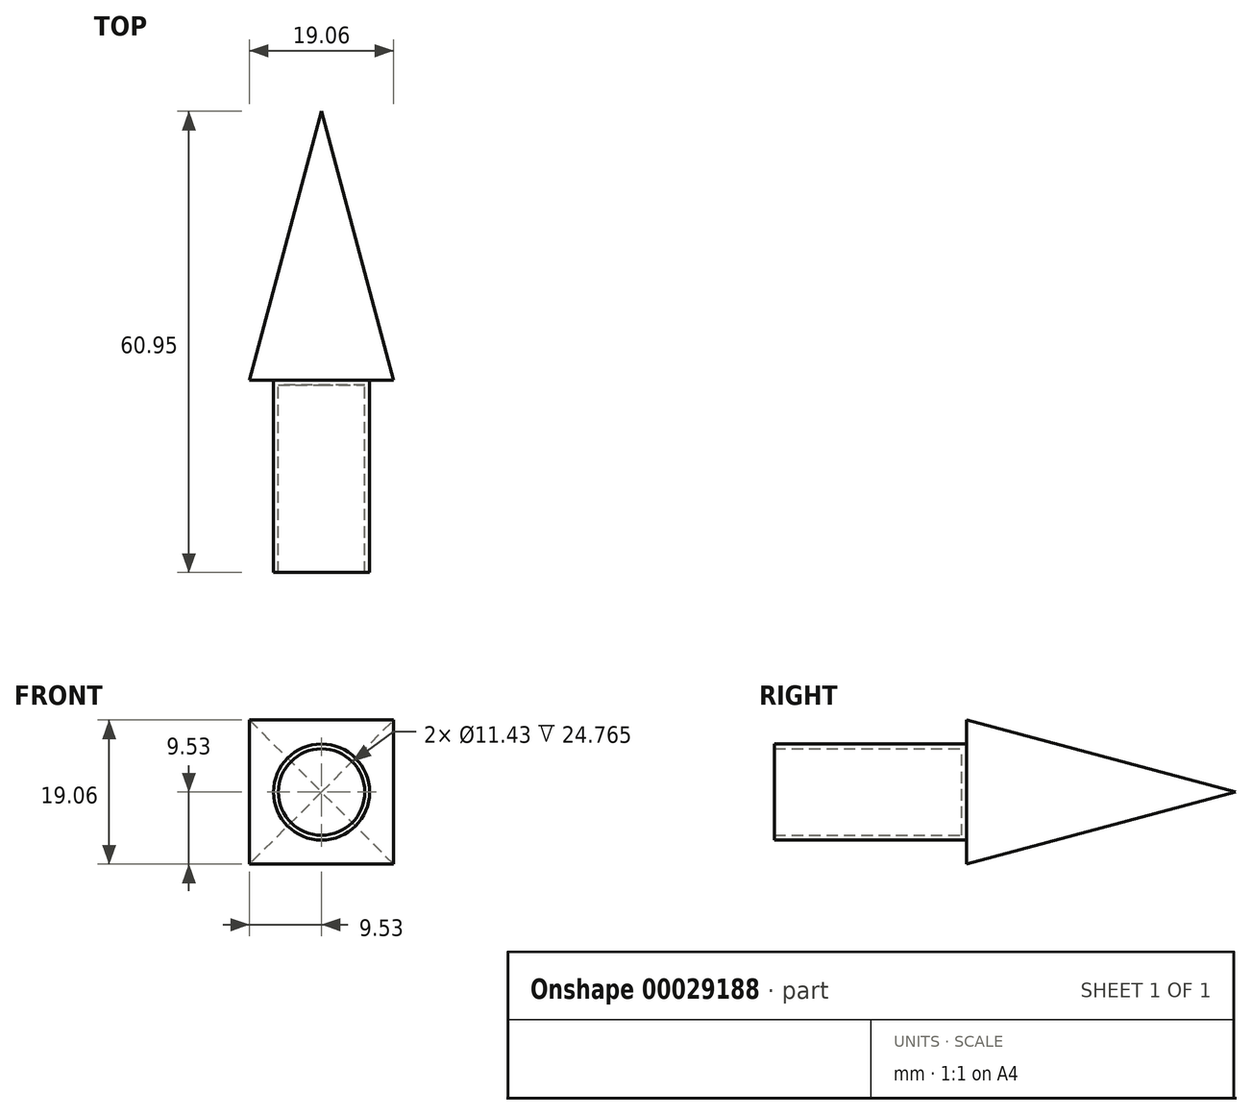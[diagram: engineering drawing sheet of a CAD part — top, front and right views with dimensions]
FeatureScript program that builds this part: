
annotation { "Feature Type Name" : "Feature", "Feature Type Description" : "" }
export const myFeature = defineFeature(function(context is Context, id is Id, definition is map)
    precondition{}
    {
        {
            var Q0;
            Q0=qCreatedBy(makeId("Front.planeOp"),FACE);
            var sketch = newSketch(context, id + "F0", { "sketchPlane" : qUnion([Q0])});
            skCircle(sketch, "E0", {"center": v(0, 0) * mm, "radius": 6.35 * mm});
            skSolve(sketch);
        }
        {
            var Q0;
            Q0=makeQuery(id+"F0.imprint","IMPRINT",FACE,{"disambiguationData":[TD([[makeQuery(id+"F0.imprint","IMPRINT",EDGE,{"derivedFrom":sQuery(id+"F0.wireOp",EDGE,"E0")}),1.0]])]});
            extrude(context, id + "F1", {"entities" : qUnion([Q0]), "depth" : 25.4 * mm});
        }
        {
            var Q0;
            Q0=makeQuery(id+"F1.opExtrude","CAP_FACE",FACE,{"disambiguationData":[OSD([sQuery(id+"F0.wireOp",EDGE,"E0")])],"isStart":false});
            shell(context, id + "F2", {"entities" : qUnion([Q0]), "thickness" : 0.64 * mm});
        }
        {
            var Q0;
            Q0=makeQuery(id+"F1.opExtrude","CAP_FACE",FACE,{"disambiguationData":[OSD([sQuery(id+"F0.wireOp",EDGE,"E0")])],"isStart":true});
            var sketch = newSketch(context, id + "F3", { "sketchPlane" : qUnion([Q0])});
            skLineSegment(sketch, "E1.rect.bottom", {"start": v(9.53, 9.52) * mm, "end": v(-9.53, 9.52) * mm});
            skLineSegment(sketch, "E1.rect.top", {"start": v(9.53, -9.53) * mm, "end": v(-9.53, -9.53) * mm});
            skLineSegment(sketch, "E1.rect.left", {"start": v(9.53, 9.52) * mm, "end": v(9.53, -9.53) * mm});
            skLineSegment(sketch, "E1.rect.right", {"start": v(-9.53, 9.52) * mm, "end": v(-9.53, -9.53) * mm});
            skPoint(sketch, "E1.rect.middle", {"position": v(0, 0) * mm});
            skSolve(sketch);
        }
        {
            var Q0;
            Q0=makeQuery(id+"F3.imprint","IMPRINT",FACE,{"disambiguationData":[TD([[makeQuery(id+"F3.imprint","IMPRINT",EDGE,{"derivedFrom":sQuery(id+"F3.wireOp",EDGE,"E1.rect.bottom")}),1.0]])]});
            var Q1;
            Q1=makeQuery(id+"F3.imprint","IMPRINT",FACE,{"disambiguationData":[TD([[makeQuery(id+"F3.imprint","IMPRINT",EDGE,{"derivedFrom":makeQuery(id+"F1.opExtrude","CAP_EDGE",EDGE,{"disambiguationData":[OSD([sQuery(id+"F0.wireOp",EDGE,"E0")])],"isStart":true})}),-1.0]])]});
            extrude(context, id + "F4", {"entities" : qUnion([Q0, Q1]), "depth" : 50.8 * mm, "hasDraft" : true, "draftAngle" : 15 * degree, "draftPullDirection" : true});
        }
    });
